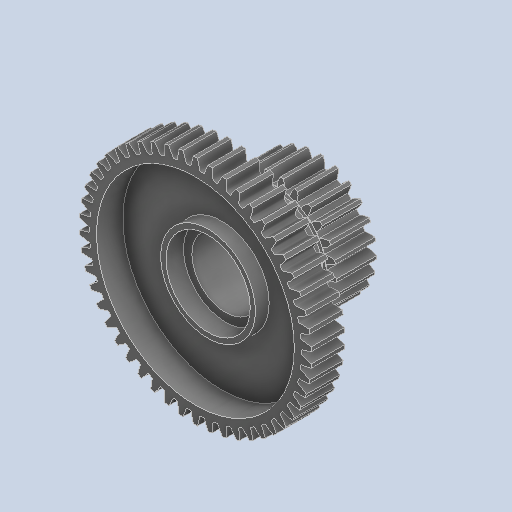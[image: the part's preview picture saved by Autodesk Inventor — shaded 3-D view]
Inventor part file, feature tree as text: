
AUTODESK INVENTOR PART (.ipt)
format: ipt  version: 2024.2 (Build 282272000, 272)  size: 585,216 bytes
history: native  units: in
note: dims shown in document units (in); Inventor stores cm internally (conversion verified against a paired STEP export)
features: chamfer x1
ambient origin geometry x8: Origin, YZ Plane, XZ Plane, XY Plane, X Axis, Y Axis, Z Axis, Center Point
bodies: Solid1 (feature_tree)
feature tree (1):
  chamfer  "Chamfer2"  [1 undecoded]
note: 1 required parameter value undecoded (feature->parameter linkage not recoverable at this tier; creation-order binding heuristic only, values carry confidence <= 0.55)
